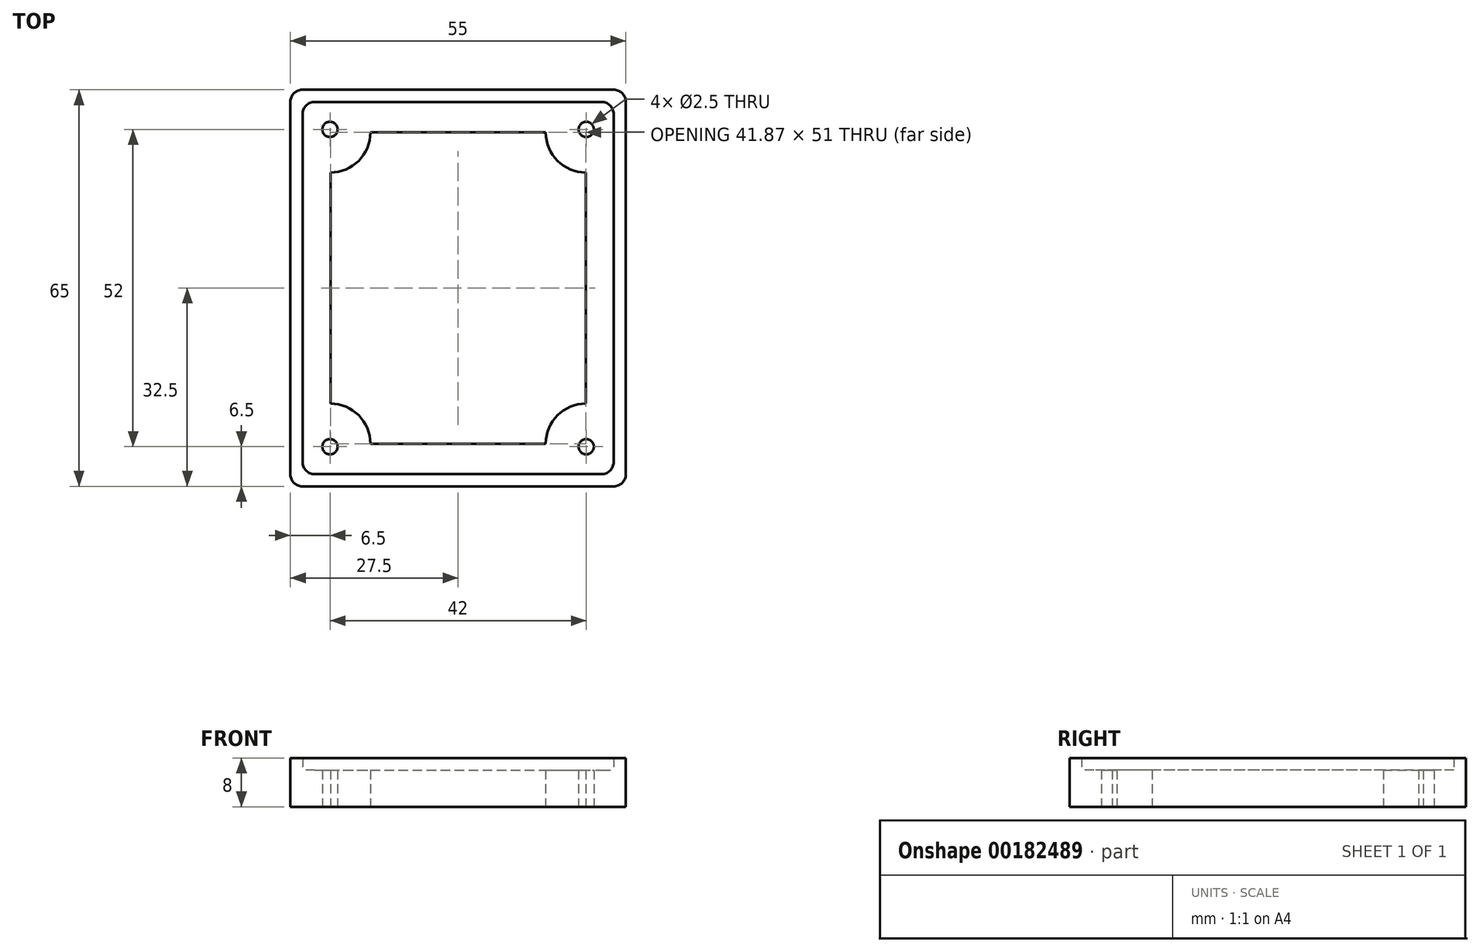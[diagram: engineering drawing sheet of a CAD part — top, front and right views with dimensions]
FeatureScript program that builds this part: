
annotation { "Feature Type Name" : "Feature", "Feature Type Description" : "" }
export const myFeature = defineFeature(function(context is Context, id is Id, definition is map)
    precondition{}
    {
        {
            var Q0;
            Q0=qCreatedBy(makeId("Top.planeOp"),FACE);
            var sketch = newSketch(context, id + "F0", { "sketchPlane" : qUnion([Q0])});
            skLineSegment(sketch, "E0.bottom", {"start": v(-20.93, 25.5) * mm, "end": v(20.93, 25.5) * mm});
            skLineSegment(sketch, "E0.top", {"start": v(-20.93, -25.5) * mm, "end": v(20.93, -25.5) * mm});
            skLineSegment(sketch, "E0.left", {"start": v(-20.93, 25.5) * mm, "end": v(-20.93, -25.5) * mm});
            skLineSegment(sketch, "E0.right", {"start": v(20.93, 25.5) * mm, "end": v(20.93, -25.5) * mm});
            skPoint(sketch, "E0.middle", {"position": v(0, 0) * mm});
            skLineSegment(sketch, "E1.bottom", {"start": v(-25.5, 30.5) * mm, "end": v(25.5, 30.5) * mm});
            skLineSegment(sketch, "E1.top", {"start": v(-25.5, -30.5) * mm, "end": v(25.5, -30.5) * mm});
            skLineSegment(sketch, "E1.left", {"start": v(-25.5, 30.5) * mm, "end": v(-25.5, -30.5) * mm});
            skLineSegment(sketch, "E1.right", {"start": v(25.5, 30.5) * mm, "end": v(25.5, -30.5) * mm});
            skLineSegment(sketch, "E2.bottom", {"start": v(-27.5, 32.5) * mm, "end": v(27.5, 32.5) * mm});
            skLineSegment(sketch, "E2.top", {"start": v(-27.5, -32.5) * mm, "end": v(27.5, -32.5) * mm});
            skLineSegment(sketch, "E2.left", {"start": v(-27.5, 32.5) * mm, "end": v(-27.5, -32.5) * mm});
            skLineSegment(sketch, "E2.right", {"start": v(27.5, 32.5) * mm, "end": v(27.5, -32.5) * mm});
            skCircle(sketch, "E3", {"center": v(-20.93, 25.5) * mm, "radius": 6.57 * mm});
            skCircle(sketch, "E4", {"center": v(20.93, 25.5) * mm, "radius": 6.57 * mm});
            skCircle(sketch, "E5", {"center": v(20.93, -25.5) * mm, "radius": 6.57 * mm});
            skCircle(sketch, "E6", {"center": v(-20.93, -25.5) * mm, "radius": 6.57 * mm});
            skSolve(sketch);
        }
        {
            var Q0;
            {var subQ4=sQuery(id+"F0.wireOp",EDGE,"E0.left");var subQ9=sQuery(id+"F0.wireOp",EDGE,"E0.bottom");var subQ10=makeQuery(id+"F0.imprint","INTERSECT",VERTEX,{"derivedFrom":[subQ9,subQ4]});Q0=makeQuery(id+"F0.imprint","IMPRINT",FACE,{"disambiguationData":[TD([[makeQuery(id+"F0.imprint","IMPRINT",EDGE,{"disambiguationData":[TD([[subQ10,-1.0]])],"derivedFrom":subQ9}),1.0]])]});}
            var Q1;
            {var subQ0=sQuery(id+"F0.wireOp",EDGE,"E0.left");var subQ1=sQuery(id+"F0.wireOp",EDGE,"E0.bottom");var subQ2=makeQuery(id+"F0.imprint","INTERSECT",VERTEX,{"derivedFrom":[subQ1,subQ0]});Q1=makeQuery(id+"F0.imprint","IMPRINT",FACE,{"disambiguationData":[TD([[makeQuery(id+"F0.imprint","IMPRINT",EDGE,{"disambiguationData":[TD([[subQ2,-1.0]])],"derivedFrom":subQ1}),-1.0]])]});}
            var Q2;
            {var subQ0=sQuery(id+"F0.wireOp",EDGE,"E3");var subQ1=sQuery(id+"F0.wireOp",EDGE,"E0.bottom");var subQ2=makeQuery(id+"F0.imprint","INTERSECT",VERTEX,{"derivedFrom":[subQ1,subQ0]});Q2=makeQuery(id+"F0.imprint","IMPRINT",FACE,{"disambiguationData":[TD([[makeQuery(id+"F0.imprint","IMPRINT",EDGE,{"disambiguationData":[TD([[subQ2,-1.0]])],"derivedFrom":subQ1}),1.0]])]});}
            var Q3;
            {var subQ4=sQuery(id+"F0.wireOp",EDGE,"E0.bottom");var subQ9=sQuery(id+"F0.wireOp",EDGE,"E0.right");var subQ10=makeQuery(id+"F0.imprint","INTERSECT",VERTEX,{"derivedFrom":[subQ4,subQ9]});Q3=makeQuery(id+"F0.imprint","IMPRINT",FACE,{"disambiguationData":[TD([[makeQuery(id+"F0.imprint","IMPRINT",EDGE,{"disambiguationData":[TD([[subQ10,1.0]])],"derivedFrom":subQ4}),1.0]])]});}
            var Q4;
            {var subQ0=sQuery(id+"F0.wireOp",EDGE,"E0.right");var subQ1=sQuery(id+"F0.wireOp",EDGE,"E0.bottom");var subQ2=makeQuery(id+"F0.imprint","INTERSECT",VERTEX,{"derivedFrom":[subQ1,subQ0]});Q4=makeQuery(id+"F0.imprint","IMPRINT",FACE,{"disambiguationData":[TD([[makeQuery(id+"F0.imprint","IMPRINT",EDGE,{"disambiguationData":[TD([[subQ2,1.0]])],"derivedFrom":subQ1}),-1.0]])]});}
            var Q5;
            {var subQ0=sQuery(id+"F0.wireOp",EDGE,"E4");var subQ1=sQuery(id+"F0.wireOp",EDGE,"E0.right");var subQ2=makeQuery(id+"F0.imprint","INTERSECT",VERTEX,{"derivedFrom":[subQ1,subQ0]});Q5=makeQuery(id+"F0.imprint","IMPRINT",FACE,{"disambiguationData":[TD([[makeQuery(id+"F0.imprint","IMPRINT",EDGE,{"disambiguationData":[TD([[subQ2,-1.0]])],"derivedFrom":subQ1}),1.0]])]});}
            var Q6;
            {var subQ0=sQuery(id+"F0.wireOp",EDGE,"E0.right");var subQ1=sQuery(id+"F0.wireOp",EDGE,"E0.top");var subQ2=makeQuery(id+"F0.imprint","INTERSECT",VERTEX,{"derivedFrom":[subQ1,subQ0]});Q6=makeQuery(id+"F0.imprint","IMPRINT",FACE,{"disambiguationData":[TD([[makeQuery(id+"F0.imprint","IMPRINT",EDGE,{"disambiguationData":[TD([[subQ2,1.0]])],"derivedFrom":subQ1}),-1.0]])]});}
            var Q7;
            {var subQ0=sQuery(id+"F0.wireOp",EDGE,"E0.right");var subQ1=sQuery(id+"F0.wireOp",EDGE,"E0.top");var subQ2=makeQuery(id+"F0.imprint","INTERSECT",VERTEX,{"derivedFrom":[subQ1,subQ0]});Q7=makeQuery(id+"F0.imprint","IMPRINT",FACE,{"disambiguationData":[TD([[makeQuery(id+"F0.imprint","IMPRINT",EDGE,{"disambiguationData":[TD([[subQ2,1.0]])],"derivedFrom":subQ1}),1.0]])]});}
            var Q8;
            {var subQ4=sQuery(id+"F0.wireOp",EDGE,"E0.left");var subQ5=sQuery(id+"F0.wireOp",EDGE,"E0.top");var subQ6=makeQuery(id+"F0.imprint","INTERSECT",VERTEX,{"derivedFrom":[subQ5,subQ4]});Q8=makeQuery(id+"F0.imprint","IMPRINT",FACE,{"disambiguationData":[TD([[makeQuery(id+"F0.imprint","IMPRINT",EDGE,{"disambiguationData":[TD([[subQ6,-1.0]])],"derivedFrom":subQ5}),-1.0]])]});}
            var Q9;
            {var subQ0=sQuery(id+"F0.wireOp",EDGE,"E0.left");var subQ1=sQuery(id+"F0.wireOp",EDGE,"E0.top");var subQ2=makeQuery(id+"F0.imprint","INTERSECT",VERTEX,{"derivedFrom":[subQ1,subQ0]});Q9=makeQuery(id+"F0.imprint","IMPRINT",FACE,{"disambiguationData":[TD([[makeQuery(id+"F0.imprint","IMPRINT",EDGE,{"disambiguationData":[TD([[subQ2,-1.0]])],"derivedFrom":subQ1}),1.0]])]});}
            var Q10;
            {var subQ0=sQuery(id+"F0.wireOp",EDGE,"E3");var subQ1=sQuery(id+"F0.wireOp",EDGE,"E0.left");var subQ2=makeQuery(id+"F0.imprint","INTERSECT",VERTEX,{"derivedFrom":[subQ1,subQ0]});Q10=makeQuery(id+"F0.imprint","IMPRINT",FACE,{"disambiguationData":[TD([[makeQuery(id+"F0.imprint","IMPRINT",EDGE,{"disambiguationData":[TD([[subQ2,-1.0]])],"derivedFrom":subQ1}),-1.0]])]});}
            var Q11;
            {var subQ0=sQuery(id+"F0.wireOp",EDGE,"E6");var subQ1=sQuery(id+"F0.wireOp",EDGE,"E0.top");var subQ2=makeQuery(id+"F0.imprint","INTERSECT",VERTEX,{"derivedFrom":[subQ1,subQ0]});Q11=makeQuery(id+"F0.imprint","IMPRINT",FACE,{"disambiguationData":[TD([[makeQuery(id+"F0.imprint","IMPRINT",EDGE,{"disambiguationData":[TD([[subQ2,-1.0]])],"derivedFrom":subQ1}),-1.0]])]});}
            var Q12;
            {var subQ0=sQuery(id+"F0.wireOp",EDGE,"E1.right");var subQ1=sQuery(id+"F0.wireOp",EDGE,"E1.bottom");var subQ2=makeQuery(id+"F0.imprint","INTERSECT",VERTEX,{"derivedFrom":[subQ1,subQ0]});Q12=makeQuery(id+"F0.imprint","IMPRINT",FACE,{"disambiguationData":[TD([[makeQuery(id+"F0.imprint","IMPRINT",EDGE,{"disambiguationData":[TD([[subQ2,1.0]])],"derivedFrom":subQ1}),-1.0]])]});}
            var Q13;
            {var subQ0=sQuery(id+"F0.wireOp",EDGE,"E1.left");var subQ1=sQuery(id+"F0.wireOp",EDGE,"E1.bottom");var subQ2=makeQuery(id+"F0.imprint","INTERSECT",VERTEX,{"derivedFrom":[subQ1,subQ0]});Q13=makeQuery(id+"F0.imprint","IMPRINT",FACE,{"disambiguationData":[TD([[makeQuery(id+"F0.imprint","IMPRINT",EDGE,{"disambiguationData":[TD([[subQ2,-1.0]])],"derivedFrom":subQ1}),-1.0]])]});}
            var Q14;
            {var subQ0=sQuery(id+"F0.wireOp",EDGE,"E1.left");var subQ1=sQuery(id+"F0.wireOp",EDGE,"E1.top");var subQ2=makeQuery(id+"F0.imprint","INTERSECT",VERTEX,{"derivedFrom":[subQ1,subQ0]});Q14=makeQuery(id+"F0.imprint","IMPRINT",FACE,{"disambiguationData":[TD([[makeQuery(id+"F0.imprint","IMPRINT",EDGE,{"disambiguationData":[TD([[subQ2,-1.0]])],"derivedFrom":subQ1}),1.0]])]});}
            var Q15;
            {var subQ0=sQuery(id+"F0.wireOp",EDGE,"E1.right");var subQ1=sQuery(id+"F0.wireOp",EDGE,"E1.top");var subQ2=makeQuery(id+"F0.imprint","INTERSECT",VERTEX,{"derivedFrom":[subQ1,subQ0]});Q15=makeQuery(id+"F0.imprint","IMPRINT",FACE,{"disambiguationData":[TD([[makeQuery(id+"F0.imprint","IMPRINT",EDGE,{"disambiguationData":[TD([[subQ2,1.0]])],"derivedFrom":subQ1}),1.0]])]});}
            extrude(context, id + "F1", {"entities" : qUnion([Q0, Q1, Q2, Q3, Q4, Q5, Q6, Q7, Q8, Q9, Q10, Q11, Q12, Q13, Q14, Q15]), "depth" : 6 * mm, "offsetDistance" : 25 * mm});
        }
        {
            var Q0;
            {var subQ5=sQuery(id+"F0.wireOp",EDGE,"E2.bottom");Q0=makeQuery(id+"F0.imprint","IMPRINT",FACE,{"disambiguationData":[TD([[makeQuery(id+"F0.imprint","IMPRINT",EDGE,{"derivedFrom":subQ5}),-1.0]])]});}
            var Q1;
            {var subQ0=sQuery(id+"F0.wireOp",EDGE,"E3");var subQ1=sQuery(id+"F0.wireOp",EDGE,"E1.bottom");var subQ2=makeQuery(id+"F0.imprint","INTERSECT",VERTEX,{"disambiguationData":[OD(0.0)],"derivedFrom":[subQ1,subQ0]});Q1=makeQuery(id+"F0.imprint","IMPRINT",FACE,{"disambiguationData":[TD([[makeQuery(id+"F0.imprint","IMPRINT",EDGE,{"disambiguationData":[TD([[subQ2,-1.0]])],"derivedFrom":subQ1}),1.0]])]});}
            var Q2;
            {var subQ0=sQuery(id+"F0.wireOp",EDGE,"E3");var subQ1=sQuery(id+"F0.wireOp",EDGE,"E1.left");var subQ2=makeQuery(id+"F0.imprint","INTERSECT",VERTEX,{"disambiguationData":[OD(0.0)],"derivedFrom":[subQ1,subQ0]});Q2=makeQuery(id+"F0.imprint","IMPRINT",FACE,{"disambiguationData":[TD([[makeQuery(id+"F0.imprint","IMPRINT",EDGE,{"disambiguationData":[TD([[subQ2,-1.0]])],"derivedFrom":subQ1}),-1.0]])]});}
            var Q3;
            {var subQ0=sQuery(id+"F0.wireOp",EDGE,"E3");var subQ1=sQuery(id+"F0.wireOp",EDGE,"E1.left");var subQ2=makeQuery(id+"F0.imprint","INTERSECT",VERTEX,{"disambiguationData":[OD(1.0)],"derivedFrom":[subQ1,subQ0]});Q3=makeQuery(id+"F0.imprint","IMPRINT",FACE,{"disambiguationData":[TD([[makeQuery(id+"F0.imprint","IMPRINT",EDGE,{"disambiguationData":[TD([[subQ2,-1.0]])],"derivedFrom":subQ1}),-1.0]])]});}
            var Q4;
            {var subQ0=sQuery(id+"F0.wireOp",EDGE,"E6");var subQ1=sQuery(id+"F0.wireOp",EDGE,"E1.left");var subQ2=makeQuery(id+"F0.imprint","INTERSECT",VERTEX,{"disambiguationData":[OD(0.0)],"derivedFrom":[subQ1,subQ0]});Q4=makeQuery(id+"F0.imprint","IMPRINT",FACE,{"disambiguationData":[TD([[makeQuery(id+"F0.imprint","IMPRINT",EDGE,{"disambiguationData":[TD([[subQ2,-1.0]])],"derivedFrom":subQ1}),-1.0]])]});}
            var Q5;
            {var subQ9=sQuery(id+"F0.wireOp",EDGE,"E2.top");Q5=makeQuery(id+"F0.imprint","IMPRINT",FACE,{"disambiguationData":[TD([[makeQuery(id+"F0.imprint","IMPRINT",EDGE,{"derivedFrom":subQ9}),1.0]])]});}
            var Q6;
            {var subQ0=sQuery(id+"F0.wireOp",EDGE,"E6");var subQ1=sQuery(id+"F0.wireOp",EDGE,"E1.top");var subQ2=makeQuery(id+"F0.imprint","INTERSECT",VERTEX,{"disambiguationData":[OD(0.0)],"derivedFrom":[subQ1,subQ0]});Q6=makeQuery(id+"F0.imprint","IMPRINT",FACE,{"disambiguationData":[TD([[makeQuery(id+"F0.imprint","IMPRINT",EDGE,{"disambiguationData":[TD([[subQ2,-1.0]])],"derivedFrom":subQ1}),-1.0]])]});}
            var Q7;
            {var subQ0=sQuery(id+"F0.wireOp",EDGE,"E5");var subQ1=sQuery(id+"F0.wireOp",EDGE,"E1.top");var subQ2=makeQuery(id+"F0.imprint","INTERSECT",VERTEX,{"disambiguationData":[OD(0.0)],"derivedFrom":[subQ1,subQ0]});Q7=makeQuery(id+"F0.imprint","IMPRINT",FACE,{"disambiguationData":[TD([[makeQuery(id+"F0.imprint","IMPRINT",EDGE,{"disambiguationData":[TD([[subQ2,-1.0]])],"derivedFrom":subQ1}),-1.0]])]});}
            var Q8;
            {var subQ0=sQuery(id+"F0.wireOp",EDGE,"E5");var subQ1=sQuery(id+"F0.wireOp",EDGE,"E1.right");var subQ2=makeQuery(id+"F0.imprint","INTERSECT",VERTEX,{"disambiguationData":[OD(0.0)],"derivedFrom":[subQ1,subQ0]});Q8=makeQuery(id+"F0.imprint","IMPRINT",FACE,{"disambiguationData":[TD([[makeQuery(id+"F0.imprint","IMPRINT",EDGE,{"disambiguationData":[TD([[subQ2,-1.0]])],"derivedFrom":subQ1}),1.0]])]});}
            var Q9;
            {var subQ0=sQuery(id+"F0.wireOp",EDGE,"E4");var subQ1=sQuery(id+"F0.wireOp",EDGE,"E1.bottom");var subQ2=makeQuery(id+"F0.imprint","INTERSECT",VERTEX,{"disambiguationData":[OD(0.0)],"derivedFrom":[subQ1,subQ0]});Q9=makeQuery(id+"F0.imprint","IMPRINT",FACE,{"disambiguationData":[TD([[makeQuery(id+"F0.imprint","IMPRINT",EDGE,{"disambiguationData":[TD([[subQ2,-1.0]])],"derivedFrom":subQ1}),1.0]])]});}
            var Q10;
            {var subQ0=sQuery(id+"F0.wireOp",EDGE,"E4");var subQ1=sQuery(id+"F0.wireOp",EDGE,"E1.right");var subQ2=makeQuery(id+"F0.imprint","INTERSECT",VERTEX,{"disambiguationData":[OD(0.0)],"derivedFrom":[subQ1,subQ0]});Q10=makeQuery(id+"F0.imprint","IMPRINT",FACE,{"disambiguationData":[TD([[makeQuery(id+"F0.imprint","IMPRINT",EDGE,{"disambiguationData":[TD([[subQ2,-1.0]])],"derivedFrom":subQ1}),1.0]])]});}
            var Q11;
            {var subQ0=sQuery(id+"F0.wireOp",EDGE,"E4");var subQ1=sQuery(id+"F0.wireOp",EDGE,"E1.right");var subQ2=makeQuery(id+"F0.imprint","INTERSECT",VERTEX,{"disambiguationData":[OD(1.0)],"derivedFrom":[subQ1,subQ0]});Q11=makeQuery(id+"F0.imprint","IMPRINT",FACE,{"disambiguationData":[TD([[makeQuery(id+"F0.imprint","IMPRINT",EDGE,{"disambiguationData":[TD([[subQ2,-1.0]])],"derivedFrom":subQ1}),1.0]])]});}
            extrude(context, id + "F2", {"entities" : qUnion([Q0, Q1, Q2, Q3, Q4, Q5, Q6, Q7, Q8, Q9, Q10, Q11]), "operationType" : NewBodyOperationType.ADD, "depth" : 8 * mm, "offsetDistance" : 25 * mm});
        }
        {
            var Q0;
            Q0=makeQuery(id+"F1.opExtrude","CAP_FACE",FACE,{"disambiguationData":[OSD([sQuery(id+"F0.wireOp",EDGE,"E0.bottom"),sQuery(id+"F0.wireOp",EDGE,"E0.top"),sQuery(id+"F0.wireOp",EDGE,"E0.left"),sQuery(id+"F0.wireOp",EDGE,"E0.right"),sQuery(id+"F0.wireOp",EDGE,"E1.bottom"),sQuery(id+"F0.wireOp",EDGE,"E1.top"),sQuery(id+"F0.wireOp",EDGE,"E1.left"),sQuery(id+"F0.wireOp",EDGE,"E1.right"),sQuery(id+"F0.wireOp",EDGE,"E3"),sQuery(id+"F0.wireOp",EDGE,"E4"),sQuery(id+"F0.wireOp",EDGE,"E5"),sQuery(id+"F0.wireOp",EDGE,"E6")])],"isStart":false});
            var sketch = newSketch(context, id + "F3", { "sketchPlane" : qUnion([Q0])});
            skLineSegment(sketch, "E7.0", {"start": v(-21, 26) * mm, "end": v(21, 26) * mm, "construction": true});
            skLineSegment(sketch, "E7.1", {"start": v(-21, 26) * mm, "end": v(-21, -26) * mm, "construction": true});
            skLineSegment(sketch, "E7.2", {"start": v(-21, -26) * mm, "end": v(21, -26) * mm, "construction": true});
            skLineSegment(sketch, "E7.3", {"start": v(21, 26) * mm, "end": v(21, -26) * mm, "construction": true});
            skSolve(sketch);
        }
        {
            var Q0;
            Q0=sQuery(id+"F3.wireOp",VERTEX,"E7.0.start");
            var Q1;
            Q1=sQuery(id+"F3.wireOp",VERTEX,"E7.0.end");
            var Q2;
            Q2=sQuery(id+"F3.wireOp",VERTEX,"E7.2.end");
            var Q3;
            Q3=sQuery(id+"F3.wireOp",VERTEX,"E7.1.end");
            var Q4;
            Q4=makeQuery(id+"F1.opExtrude","SWEPT_BODY",BODY,{"disambiguationData":[OSD([sQuery(id+"F0.wireOp",EDGE,"E0.bottom"),sQuery(id+"F0.wireOp",EDGE,"E0.top"),sQuery(id+"F0.wireOp",EDGE,"E0.left"),sQuery(id+"F0.wireOp",EDGE,"E0.right"),sQuery(id+"F0.wireOp",EDGE,"E1.bottom"),sQuery(id+"F0.wireOp",EDGE,"E1.top"),sQuery(id+"F0.wireOp",EDGE,"E1.left"),sQuery(id+"F0.wireOp",EDGE,"E1.right"),sQuery(id+"F0.wireOp",EDGE,"E3"),sQuery(id+"F0.wireOp",EDGE,"E4"),sQuery(id+"F0.wireOp",EDGE,"E5"),sQuery(id+"F0.wireOp",EDGE,"E6")])]});
            hole(context, id + "F4", {"style" : HoleStyle.SIMPLE, "endStyle" : HoleEndStyle.BLIND, "holeDiameter" : 2.5 * mm, "majorDiameter" : 5 * mm, "holeDepth" : 150 * mm, "tappedDepth" : 12 * mm, "tapClearance" : 3, "locations" : qUnion([Q0, Q1, Q2, Q3]), "scope" : qUnion([Q4])});
        }
        {
            var Q0;
            Q0=makeQuery(id+"F2.opExtrude","SWEPT_EDGE",EDGE,{"disambiguationData":[OSD([sQuery(id+"F0.wireOp",EDGE,"E1.bottom"),sQuery(id+"F0.wireOp",EDGE,"E1.right")])]});
            var Q1;
            Q1=makeQuery(id+"F2.opExtrude","SWEPT_EDGE",EDGE,{"disambiguationData":[OSD([sQuery(id+"F0.wireOp",EDGE,"E1.top"),sQuery(id+"F0.wireOp",EDGE,"E1.right")])]});
            var Q2;
            Q2=makeQuery(id+"F2.opExtrude","SWEPT_EDGE",EDGE,{"disambiguationData":[OSD([sQuery(id+"F0.wireOp",EDGE,"E1.top"),sQuery(id+"F0.wireOp",EDGE,"E1.left")])]});
            var Q3;
            Q3=makeQuery(id+"F2.opExtrude","SWEPT_EDGE",EDGE,{"disambiguationData":[OSD([sQuery(id+"F0.wireOp",EDGE,"E1.bottom"),sQuery(id+"F0.wireOp",EDGE,"E1.left")])]});
            var Q4;
            Q4=makeQuery(id+"F2.opExtrude","SWEPT_EDGE",EDGE,{"disambiguationData":[OSD([sQuery(id+"F0.wireOp",EDGE,"E2.bottom"),sQuery(id+"F0.wireOp",EDGE,"E2.right")])]});
            var Q5;
            Q5=makeQuery(id+"F2.opExtrude","SWEPT_EDGE",EDGE,{"disambiguationData":[OSD([sQuery(id+"F0.wireOp",EDGE,"E2.top"),sQuery(id+"F0.wireOp",EDGE,"E2.right")])]});
            var Q6;
            Q6=makeQuery(id+"F2.opExtrude","SWEPT_EDGE",EDGE,{"disambiguationData":[OSD([sQuery(id+"F0.wireOp",EDGE,"E2.top"),sQuery(id+"F0.wireOp",EDGE,"E2.left")])]});
            var Q7;
            Q7=makeQuery(id+"F2.opExtrude","SWEPT_EDGE",EDGE,{"disambiguationData":[OSD([sQuery(id+"F0.wireOp",EDGE,"E2.bottom"),sQuery(id+"F0.wireOp",EDGE,"E2.left")])]});
            fillet(context, id + "F5", {"entities" : qUnion([Q0, Q1, Q2, Q3, Q4, Q5, Q6, Q7]), "tangentPropagation" : true, "radius" : 2 * mm, "defaultsChanged" : false, "vertexSettings" : [], "allowEdgeOverflow" : false});
        }
    });
